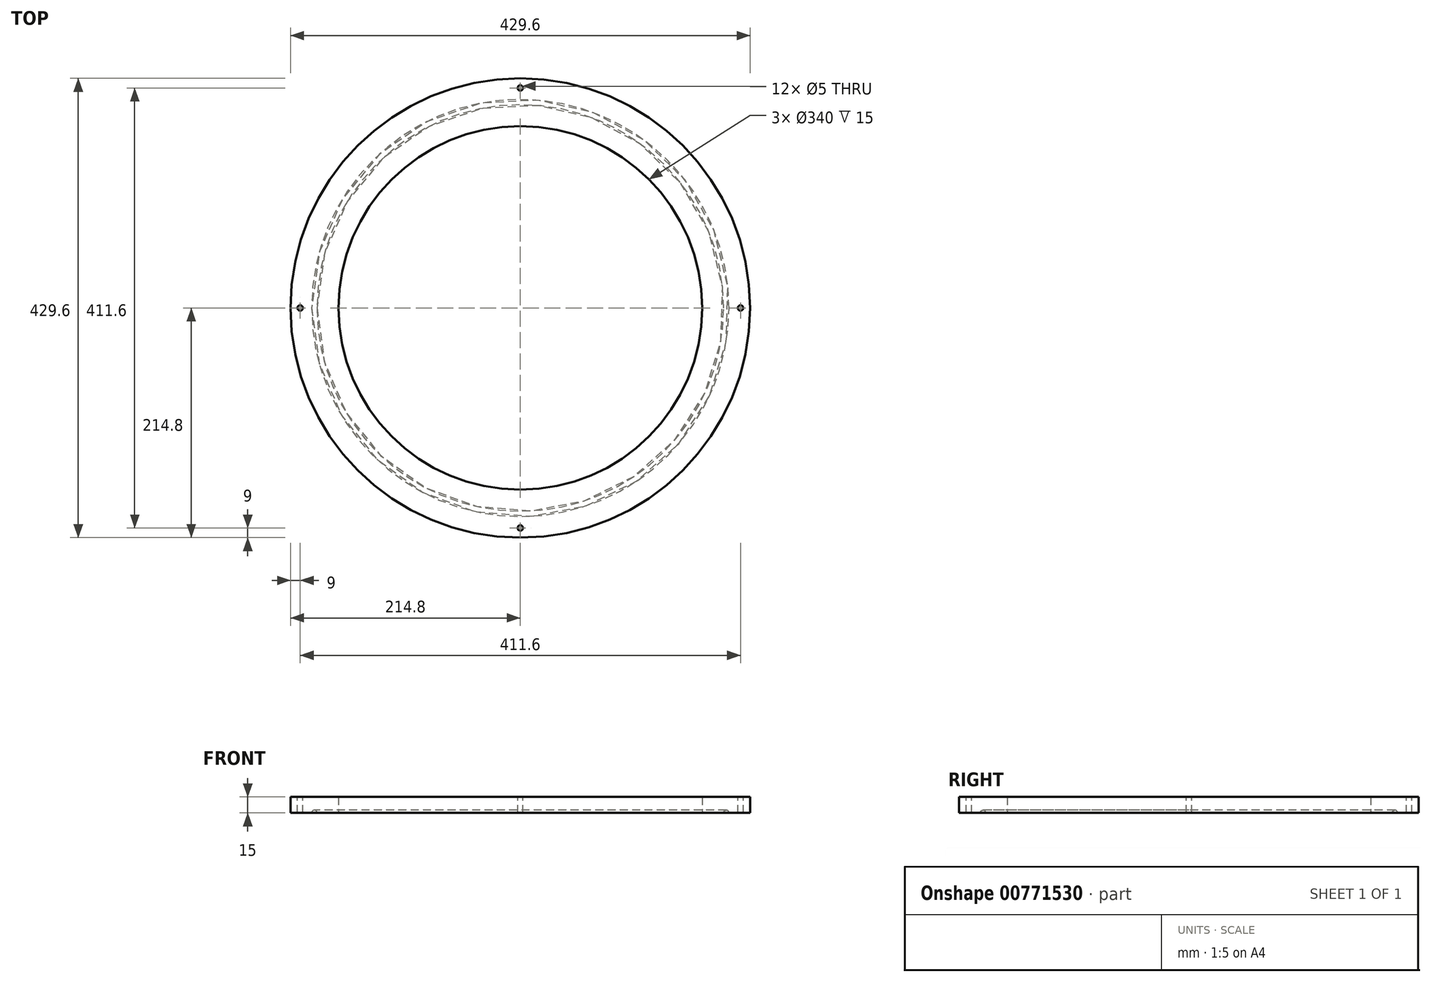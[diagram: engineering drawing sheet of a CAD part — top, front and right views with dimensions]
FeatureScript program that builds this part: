
annotation { "Feature Type Name" : "Feature", "Feature Type Description" : "" }
export const myFeature = defineFeature(function(context is Context, id is Id, definition is map)
    precondition{}
    {
        {
            var Q0;
            Q0=qCreatedBy(makeId("Front.planeOp"),FACE);
            var sketch = newSketch(context, id + "F0", { "sketchPlane" : qUnion([Q0])});
            skLineSegment(sketch, "E0", {"start": v(214.8, 0) * mm, "end": v(214.8, 15) * mm});
            skLineSegment(sketch, "E1", {"start": v(214.8, 15) * mm, "end": v(170, 15) * mm});
            skLineSegment(sketch, "E2", {"start": v(170, 15) * mm, "end": v(170, 0) * mm});
            skLineSegment(sketch, "E3", {"start": v(0, 0) * mm, "end": v(0, 39) * mm});
            skLineSegment(sketch, "E4", {"start": v(170, 0) * mm, "end": v(190, 0) * mm});
            skLineSegment(sketch, "E5", {"start": v(214.8, 0) * mm, "end": v(195, 0) * mm});
            skArc(sketch, "E6", {"start": v(195, 0) * mm, "mid": v(192.5, 2.6) * mm, "end": v(190, 0) * mm});
            skSolve(sketch);
        }
        {
            var Q0;
            Q0 = qSketchRegion(id + "F0", true);
            var Q1;
            Q1=sQuery(id+"F0.wireOp",EDGE,"E3");
            revolve(context, id + "F1", {"surfaceOperationType" : NewSurfaceOperationType.NEW, "entities" : qUnion([Q0]), "axis" : qUnion([Q1]), "revolveType" : RevolveType.FULL});
        }
        {
            var Q0;
            Q0=makeQuery(id+"F1.opRevolve","SWEPT_FACE",FACE,{"disambiguationData":[OSD([sQuery(id+"F0.wireOp",EDGE,"E1")])]});
            var sketch = newSketch(context, id + "F2", { "sketchPlane" : qUnion([Q0])});
            skCircle(sketch, "E7", {"center": v(205.8, 0) * mm, "radius": 2.5 * mm});
            skCircle(sketch, "E8", {"center": v(0, 205.8) * mm, "radius": 2.5 * mm});
            skCircle(sketch, "E9", {"center": v(-205.8, 0) * mm, "radius": 2.5 * mm});
            skCircle(sketch, "E10", {"center": v(0, -205.8) * mm, "radius": 2.5 * mm});
            skSolve(sketch);
        }
        {
            var Q0;
            Q0 = qSketchRegion(id + "F2", true);
            extrude(context, id + "F3", {"entities" : qUnion([Q0]), "operationType" : NewBodyOperationType.REMOVE, "oppositeDirection" : true, "depth" : 25 * mm, "offsetDistance" : 25 * mm});
        }
    });
